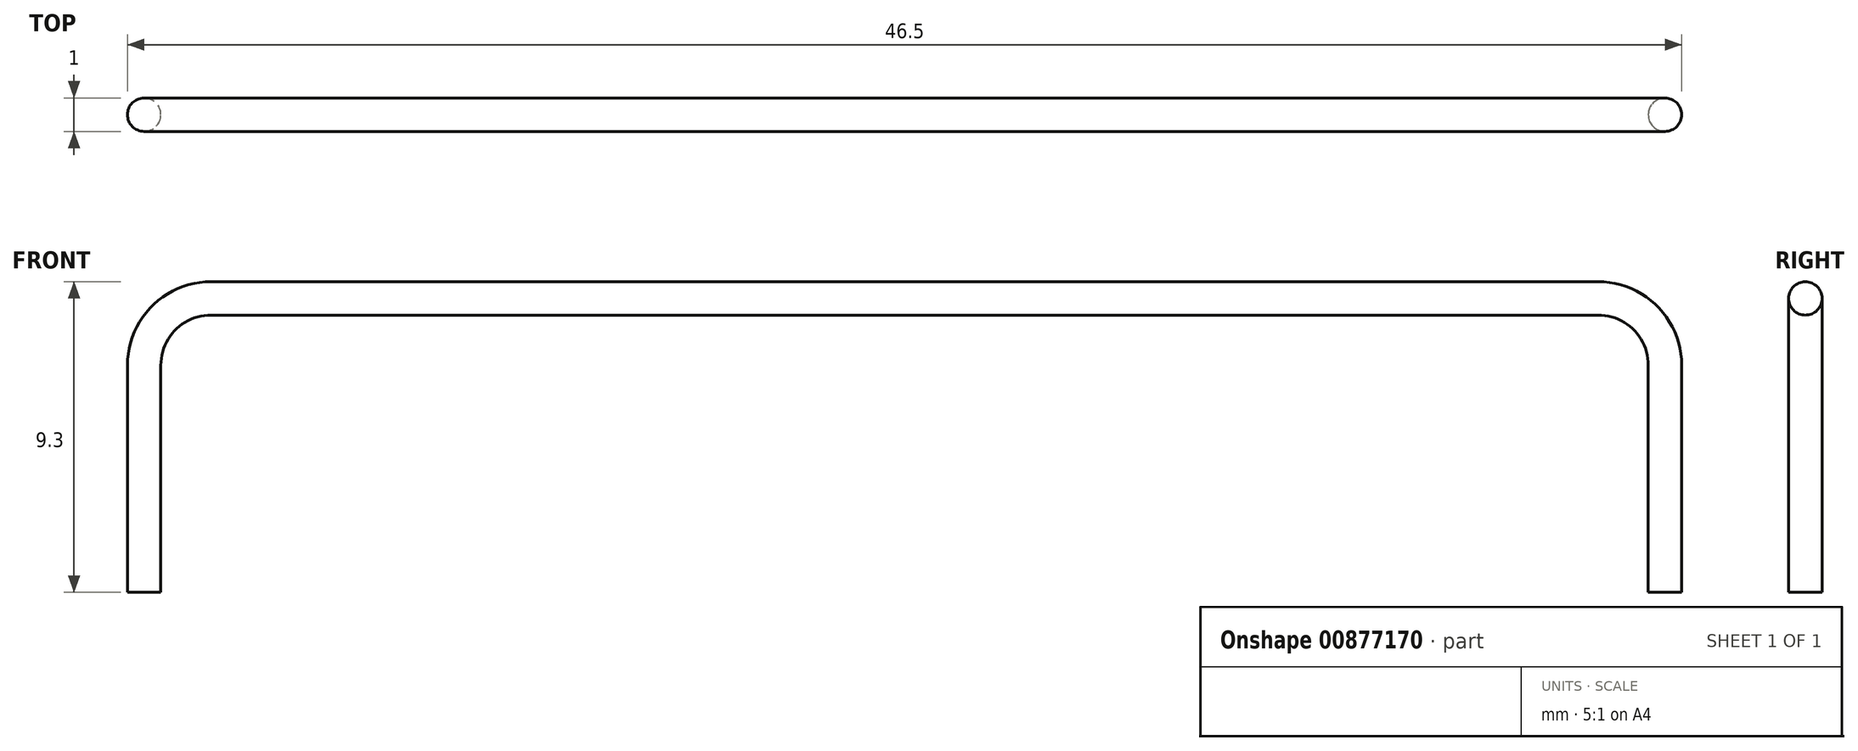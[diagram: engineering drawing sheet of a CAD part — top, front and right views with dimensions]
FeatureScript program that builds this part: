
annotation { "Feature Type Name" : "Feature", "Feature Type Description" : "" }
export const myFeature = defineFeature(function(context is Context, id is Id, definition is map)
    precondition{}
    {
        {
            var Q0;
            Q0=qCreatedBy(makeId("Front.planeOp"),FACE);
            var sketch = newSketch(context, id + "F0", { "sketchPlane" : qUnion([Q0])});
            skLineSegment(sketch, "E0", {"start": v(0, 0) * mm, "end": v(20.75, 0) * mm});
            skLineSegment(sketch, "E1", {"start": v(22.75, -2) * mm, "end": v(22.75, -8.8) * mm});
            skArc(sketch, "E2", {"start": v(22.75, -2) * mm, "mid": v(22.16, -0.59) * mm, "end": v(20.75, 0) * mm});
            skSolve(sketch);
        }
        {
            var Q0;
            Q0=qCreatedBy(makeId("Right.planeOp"),FACE);
            var sketch = newSketch(context, id + "F1", { "sketchPlane" : qUnion([Q0])});
            skCircle(sketch, "E3", {"center": v(0, 0) * mm, "radius": 0.5 * mm});
            skSolve(sketch);
        }
        {
            var Q0;
            Q0=makeQuery(id+"F1.imprint","IMPRINT",FACE,{"disambiguationData":[TD([[makeQuery(id+"F1.imprint","IMPRINT",EDGE,{"derivedFrom":sQuery(id+"F1.wireOp",EDGE,"E3")}),1.0]])]});
            var Q1;
            Q1=sQuery(id+"F0.wireOp",EDGE,"E0");
            var Q2;
            Q2=sQuery(id+"F0.wireOp",EDGE,"E2");
            var Q3;
            Q3=sQuery(id+"F0.wireOp",EDGE,"E1");
            sweep(context, id + "F2", {"profiles" : qUnion([Q0]), "path" : qUnion([Q1, Q2, Q3])});
        }
        {
            var Q0;
            Q0=makeQuery(id+"F2.opSweep","SWEPT_BODY",BODY,{"disambiguationData":[OSD([sQuery(id+"F0.wireOp",EDGE,"E1"),sQuery(id+"F1.wireOp",EDGE,"E3")])]});
            var Q1;
            Q1=makeQuery(id+"F2.opSweep","CAP_FACE",FACE,{"disambiguationData":[OSD([sQuery(id+"F0.wireOp",VERTEX,"E0.start"),sQuery(id+"F1.wireOp",EDGE,"E3")])],"isStart":true});
            mirror(context, id + "F3", {"operationType" : NewBodyOperationType.ADD, "entities" : qUnion([Q0]), "mirrorPlane" : qUnion([Q1])});
        }
    });
